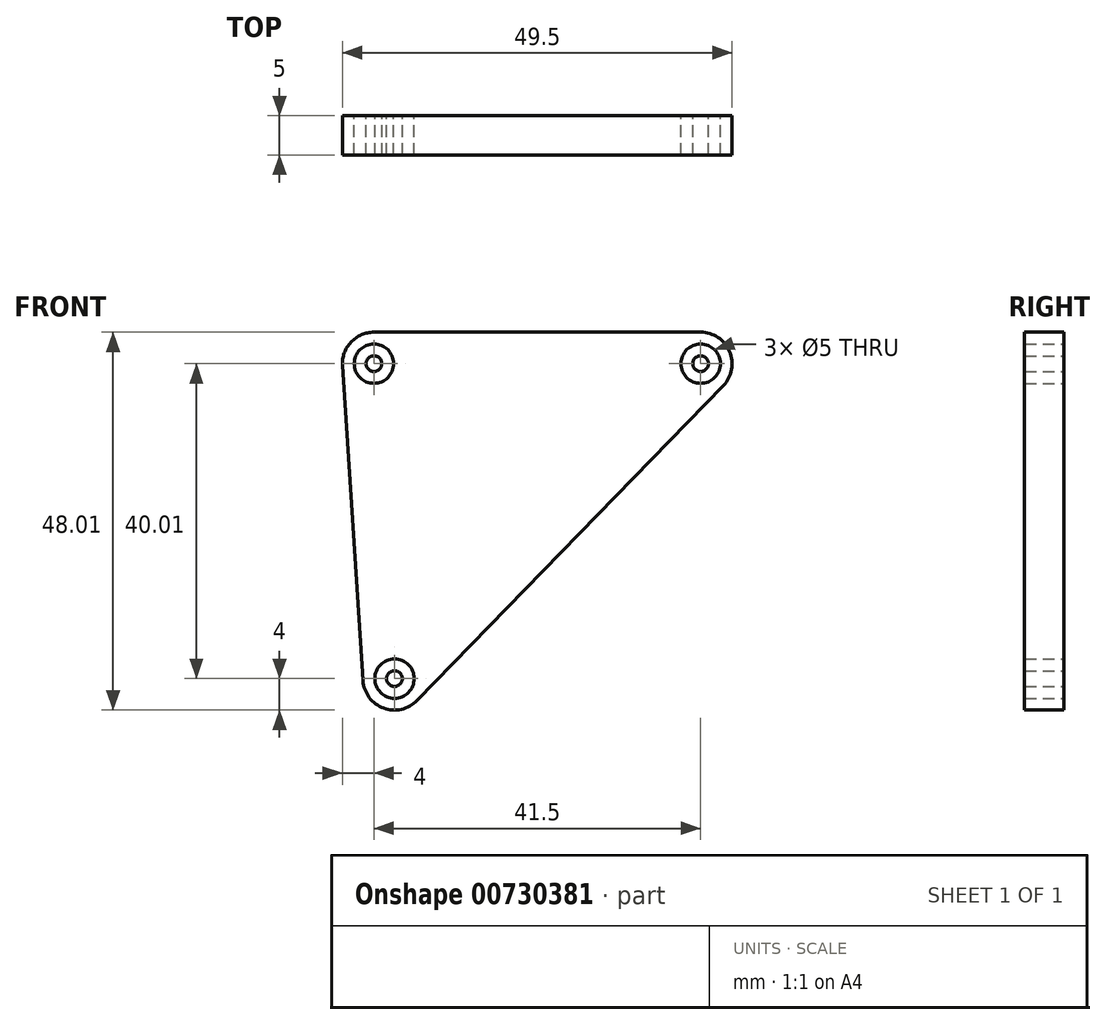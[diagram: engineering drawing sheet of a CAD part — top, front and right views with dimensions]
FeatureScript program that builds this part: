
annotation { "Feature Type Name" : "Feature", "Feature Type Description" : "" }
export const myFeature = defineFeature(function(context is Context, id is Id, definition is map)
    precondition{}
    {
        {
            var Q0;
            Q0=qCreatedBy(makeId("Front.planeOp"),FACE);
            var sketch = newSketch(context, id + "F0", { "sketchPlane" : qUnion([Q0])});
            skArc(sketch, "E0", {"start": v(-15.71, 6.74) * mm, "mid": v(-18.63, 5.47) * mm, "end": v(-19.7, 2.48) * mm});
            skArc(sketch, "E1", {"start": v(28.66, -0.05) * mm, "mid": v(29.47, 4.3) * mm, "end": v(25.79, 6.74) * mm});
            skArc(sketch, "E2", {"start": v(-17.1, -37.53) * mm, "mid": v(-14.48, -41.02) * mm, "end": v(-10.23, -40.06) * mm});
            skLineSegment(sketch, "E3", {"start": v(-15.71, 6.74) * mm, "end": v(25.79, 6.74) * mm});
            skLineSegment(sketch, "E4", {"start": v(-19.7, 2.48) * mm, "end": v(-17.1, -37.53) * mm});
            skLineSegment(sketch, "E5", {"start": v(28.66, -0.05) * mm, "end": v(-10.23, -40.06) * mm});
            skCircle(sketch, "E6", {"center": v(-15.71, 2.74) * mm, "radius": 2.5 * mm});
            skCircle(sketch, "E7", {"center": v(-15.71, 2.74) * mm, "radius": 1 * mm});
            skCircle(sketch, "E8", {"center": v(25.79, 2.74) * mm, "radius": 2.5 * mm});
            skCircle(sketch, "E9", {"center": v(25.79, 2.74) * mm, "radius": 1 * mm});
            skCircle(sketch, "E10", {"center": v(-13.1, -37.27) * mm, "radius": 2.5 * mm});
            skCircle(sketch, "E11", {"center": v(-13.1, -37.27) * mm, "radius": 1 * mm});
            skSolve(sketch);
        }
        {
            var Q0;
            Q0 = qSketchRegion(id + "F0", true);
            var Q1;
            Q1=makeQuery(id+"F0.imprint","IMPRINT",FACE,{"disambiguationData":[TD([[makeQuery(id+"F0.imprint","IMPRINT",EDGE,{"derivedFrom":sQuery(id+"F0.wireOp",EDGE,"E7")}),1.0]])]});
            var Q2;
            Q2=makeQuery(id+"F0.imprint","IMPRINT",FACE,{"disambiguationData":[TD([[makeQuery(id+"F0.imprint","IMPRINT",EDGE,{"derivedFrom":sQuery(id+"F0.wireOp",EDGE,"E9")}),1.0]])]});
            var Q3;
            Q3=makeQuery(id+"F0.imprint","IMPRINT",FACE,{"disambiguationData":[TD([[makeQuery(id+"F0.imprint","IMPRINT",EDGE,{"derivedFrom":sQuery(id+"F0.wireOp",EDGE,"E11")}),1.0]])]});
            extrude(context, id + "F1", {"entities" : qUnion([Q0, Q1, Q2, Q3]), "depth" : 5 * mm, "offsetDistance" : 25 * mm});
        }
    });
